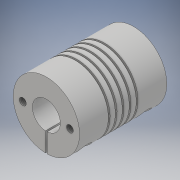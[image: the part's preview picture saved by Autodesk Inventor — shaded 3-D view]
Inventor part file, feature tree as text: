
AUTODESK INVENTOR PART (.ipt)
format: ipt  version: 2017 (Build 210142000, 142)  size: 280,064 bytes
history: native  units: mm
features: extrude x10, sketch x10, other x5, mirror x4, thread x4, pattern_linear x2, pattern_circular x1
ambient origin geometry x8: Origin, YZ Plane, XZ Plane, XY Plane, X Axis, Y Axis, Z Axis, Center Point
bodies: Body1 (feature_tree)
feature tree (36):
  other  "Твердое тело1"
  extrude  "Выдавливание1"  Depth=19.0mm
  extrude  "Выдавливание2"  Depth=25.0mm TaperAngle=0.0deg
  extrude  "Выдавливание3"  Depth=6.0mm
  other  "РабПлоскость1"
  other  "РабПлоскость2"
  extrude  "Выдавливание5"  Depth=12.5mm TaperAngle=0.0deg
  pattern_linear  "Прямоуг.массив2"  Spacing1=8.0mm  [1 undecoded]
  pattern_linear  "Прямоуг.массив3"  Spacing1=12.5mm  [1 undecoded]
  extrude  "Выдавливание6"  [1 undecoded]
  extrude  "Выдавливание7"  Depth=19.0mm
  pattern_circular  "Круговой массив2"  [2 undecoded]
  mirror  "Зеркальное отражение2"
  thread  "Резьба1"
  thread  "Резьба2"
  thread  "Резьба3"
  thread  "Резьба4"
  mirror  "Зеркальное отражение3"
  other  "РабПлоскость3"
  extrude  "Выдавливание8"  Depth=0.5mm TaperAngle=0.0deg
  extrude  "Выдавливание9"  Depth=2.0mm
  other  "РабПлоскость5"
  extrude  "Выдавливание10"  Depth=2.0mm
  extrude  "Выдавливание11"  Depth=0.5mm TaperAngle=0.0deg
  mirror  "Зеркальное отражение10"
  mirror  "Зеркальное отражение11"
  sketch  "Эскиз1"
  sketch  "Эскиз2"
  sketch  "Эскиз3"
  sketch  "Эскиз5"
  sketch  "Эскиз6"
  sketch  "Эскиз7"
  sketch  "Эскиз8"
  sketch  "Эскиз9"
  sketch  "Эскиз10"
  sketch  "Эскиз11"
note: 5 required parameter values undecoded (feature->parameter linkage not recoverable at this tier; creation-order binding heuristic only, values carry confidence <= 0.55)
